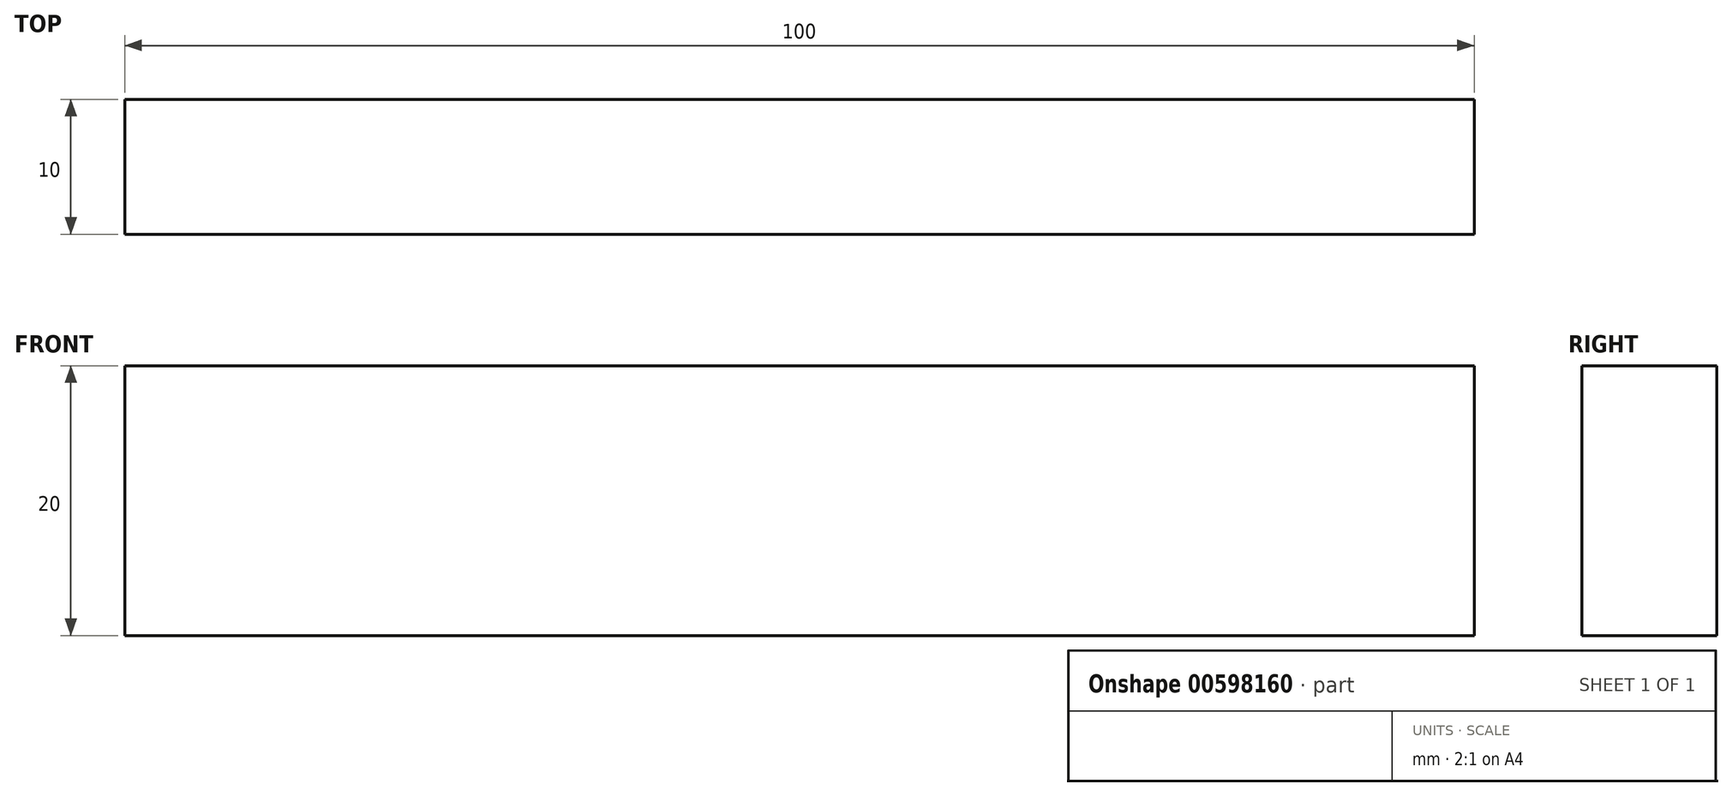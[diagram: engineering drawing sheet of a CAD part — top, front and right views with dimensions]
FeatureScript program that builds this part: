
annotation { "Feature Type Name" : "Feature", "Feature Type Description" : "" }
export const myFeature = defineFeature(function(context is Context, id is Id, definition is map)
    precondition{}
    {
        {
            var Q0;
            Q0=qCreatedBy(makeId("Front.planeOp"),FACE);
            var sketch = newSketch(context, id + "F0", { "sketchPlane" : qUnion([Q0])});
            skLineSegment(sketch, "E0.bottom", {"start": v(0, 0) * mm, "end": v(100, 0) * mm});
            skLineSegment(sketch, "E0.top", {"start": v(0, 20) * mm, "end": v(100, 20) * mm});
            skLineSegment(sketch, "E0.left", {"start": v(0, 0) * mm, "end": v(0, 20) * mm});
            skLineSegment(sketch, "E0.right", {"start": v(100, 0) * mm, "end": v(100, 20) * mm});
            skSolve(sketch);
        }
        {
            var Q0;
            Q0 = qSketchRegion(id + "F0", true);
            extrude(context, id + "F1", {"entities" : qUnion([Q0]), "depth" : 10 * mm, "offsetDistance" : 25 * mm});
        }
    });
